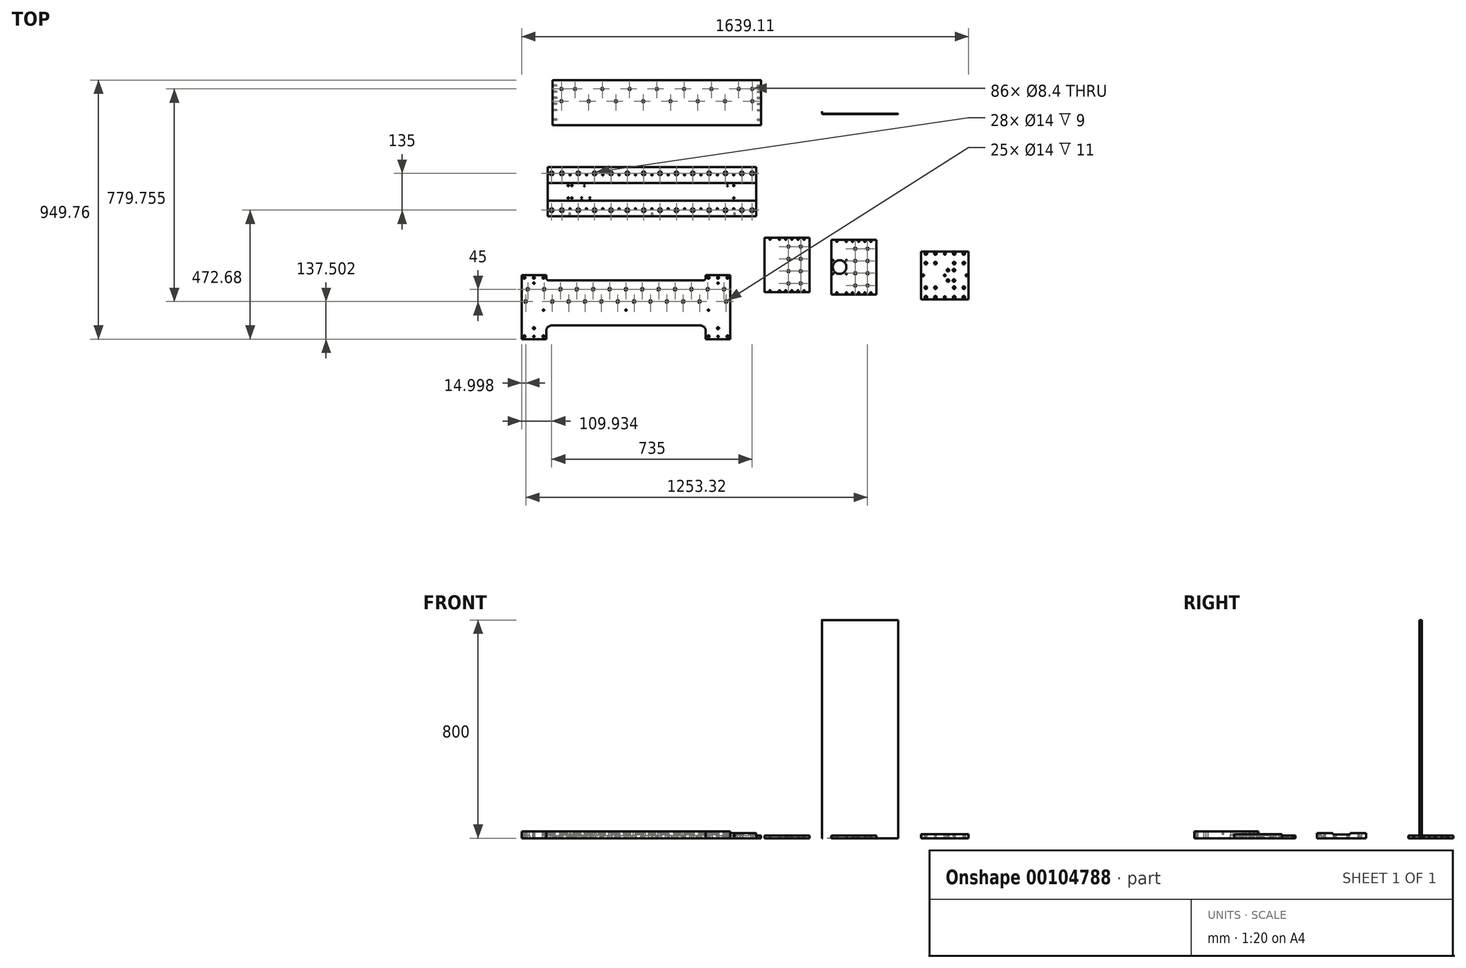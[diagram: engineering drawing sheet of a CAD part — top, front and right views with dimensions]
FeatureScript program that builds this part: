
annotation { "Feature Type Name" : "Feature", "Feature Type Description" : "" }
export const myFeature = defineFeature(function(context is Context, id is Id, definition is map)
    precondition{}
    {
        {
            var Q0;
            Q0=qCreatedBy(makeId("Top.planeOp"),FACE);
            var sketch = newSketch(context, id + "F0", { "sketchPlane" : qUnion([Q0])});
            skLineSegment(sketch, "E0.bottom", {"start": v(-320.38, 63) * mm, "end": v(444.62, 63) * mm});
            skLineSegment(sketch, "E0.top", {"start": v(-320.38, -117) * mm, "end": v(444.62, -117) * mm});
            skLineSegment(sketch, "E0.left", {"start": v(-320.38, 63) * mm, "end": v(-320.38, -117) * mm});
            skLineSegment(sketch, "E0.right", {"start": v(444.62, 63) * mm, "end": v(444.62, -117) * mm});
            skLineSegment(sketch, "E1.right", {"start": v(462.93, 382.58) * mm, "end": v(462.93, 217.58) * mm});
            skLineSegment(sketch, "E1.left", {"start": v(-302.07, 382.58) * mm, "end": v(-302.07, 217.58) * mm});
            skLineSegment(sketch, "E1.top", {"start": v(-302.07, 217.58) * mm, "end": v(462.93, 217.58) * mm});
            skLineSegment(sketch, "E1.bottom", {"start": v(-302.07, 382.58) * mm, "end": v(462.93, 382.58) * mm});
            skLineSegment(sketch, "E2.bottom", {"start": v(475.41, -195.5) * mm, "end": v(640.41, -195.5) * mm});
            skLineSegment(sketch, "E2.top", {"start": v(475.41, -395.5) * mm, "end": v(640.41, -395.5) * mm});
            skLineSegment(sketch, "E2.left", {"start": v(475.41, -195.5) * mm, "end": v(475.41, -395.5) * mm});
            skLineSegment(sketch, "E2.right", {"start": v(640.41, -195.5) * mm, "end": v(640.41, -395.5) * mm});
            skCircle(sketch, "E3", {"center": v(575.41, -200.5) * mm, "radius": 2.65 * mm});
            skCircle(sketch, "E4", {"center": v(620.41, -200.5) * mm, "radius": 2.65 * mm});
            skCircle(sketch, "E5", {"center": v(597.91, -200.5) * mm, "radius": 2.65 * mm});
            skCircle(sketch, "E6", {"center": v(552.91, -200.5) * mm, "radius": 2.65 * mm});
            skCircle(sketch, "E7", {"center": v(495.41, -200.5) * mm, "radius": 2.65 * mm});
            skCircle(sketch, "E8", {"center": v(530.41, -200.5) * mm, "radius": 2.65 * mm});
            skCircle(sketch, "E9", {"center": v(575.41, -390.5) * mm, "radius": 2.65 * mm});
            skCircle(sketch, "E10", {"center": v(552.91, -390.5) * mm, "radius": 2.65 * mm});
            skCircle(sketch, "E11", {"center": v(597.91, -390.5) * mm, "radius": 2.65 * mm});
            skCircle(sketch, "E12", {"center": v(620.41, -390.5) * mm, "radius": 2.65 * mm});
            skCircle(sketch, "E13", {"center": v(530.41, -390.5) * mm, "radius": 2.65 * mm});
            skCircle(sketch, "E14", {"center": v(495.41, -390.5) * mm, "radius": 2.65 * mm});
            skLineSegment(sketch, "E15.top", {"start": v(720.5, -403.15) * mm, "end": v(885.5, -403.15) * mm});
            skLineSegment(sketch, "E15.bottom", {"start": v(720.5, -203.15) * mm, "end": v(885.5, -203.15) * mm});
            skLineSegment(sketch, "E15.right", {"start": v(885.5, -203.15) * mm, "end": v(885.5, -403.15) * mm});
            skLineSegment(sketch, "E15.left", {"start": v(720.5, -203.15) * mm, "end": v(720.5, -403.15) * mm});
            skCircle(sketch, "E16", {"center": v(843, -208.15) * mm, "radius": 2.65 * mm});
            skCircle(sketch, "E17", {"center": v(798, -398.15) * mm, "radius": 2.65 * mm});
            skCircle(sketch, "E18", {"center": v(865.5, -208.15) * mm, "radius": 2.65 * mm});
            skCircle(sketch, "E19", {"center": v(843, -398.15) * mm, "radius": 2.65 * mm});
            skCircle(sketch, "E20", {"center": v(775.5, -208.15) * mm, "radius": 2.65 * mm});
            skCircle(sketch, "E21", {"center": v(865.5, -398.15) * mm, "radius": 2.65 * mm});
            skCircle(sketch, "E22", {"center": v(798, -208.15) * mm, "radius": 2.65 * mm});
            skCircle(sketch, "E23", {"center": v(775.5, -398.15) * mm, "radius": 2.65 * mm});
            skCircle(sketch, "E24", {"center": v(740.5, -398.15) * mm, "radius": 2.65 * mm});
            skCircle(sketch, "E25", {"center": v(740.5, -208.15) * mm, "radius": 2.65 * mm});
            skCircle(sketch, "E26", {"center": v(820.5, -398.15) * mm, "radius": 2.65 * mm});
            skCircle(sketch, "E27", {"center": v(820.5, -208.15) * mm, "radius": 2.65 * mm});
            skCircle(sketch, "E28", {"center": v(-237.88, -89.5) * mm, "radius": 2.5 * mm});
            skCircle(sketch, "E29", {"center": v(-177.88, -89.5) * mm, "radius": 2.5 * mm});
            skCircle(sketch, "E30", {"center": v(-117.88, -89.5) * mm, "radius": 2.5 * mm});
            skCircle(sketch, "E31", {"center": v(-57.88, -89.5) * mm, "radius": 2.5 * mm});
            skCircle(sketch, "E32", {"center": v(2.12, -89.5) * mm, "radius": 2.5 * mm});
            skCircle(sketch, "E33", {"center": v(62.12, -89.5) * mm, "radius": 2.5 * mm});
            skCircle(sketch, "E34", {"center": v(122.12, -89.5) * mm, "radius": 2.5 * mm});
            skCircle(sketch, "E35", {"center": v(182.12, -89.5) * mm, "radius": 2.5 * mm});
            skCircle(sketch, "E36", {"center": v(242.12, -89.5) * mm, "radius": 2.5 * mm});
            skCircle(sketch, "E37", {"center": v(302.12, -89.5) * mm, "radius": 2.5 * mm});
            skCircle(sketch, "E38", {"center": v(362.12, -89.5) * mm, "radius": 2.5 * mm});
            skCircle(sketch, "E39", {"center": v(-117.88, 35.5) * mm, "radius": 2.5 * mm});
            skCircle(sketch, "E40", {"center": v(-57.88, 35.5) * mm, "radius": 2.5 * mm});
            skCircle(sketch, "E41", {"center": v(182.12, 35.5) * mm, "radius": 2.5 * mm});
            skCircle(sketch, "E42", {"center": v(2.12, 35.5) * mm, "radius": 2.5 * mm});
            skCircle(sketch, "E43", {"center": v(62.12, 35.5) * mm, "radius": 2.5 * mm});
            skCircle(sketch, "E44", {"center": v(302.12, 35.5) * mm, "radius": 2.5 * mm});
            skCircle(sketch, "E45", {"center": v(-177.88, 35.5) * mm, "radius": 2.5 * mm});
            skCircle(sketch, "E46", {"center": v(362.12, 35.5) * mm, "radius": 2.5 * mm});
            skCircle(sketch, "E47", {"center": v(122.12, 35.5) * mm, "radius": 2.5 * mm});
            skCircle(sketch, "E48", {"center": v(242.12, 35.5) * mm, "radius": 2.5 * mm});
            skCircle(sketch, "E49", {"center": v(-237.88, 35.5) * mm, "radius": 2.5 * mm});
            skCircle(sketch, "E50", {"center": v(362.62, -4) * mm, "radius": 2.5 * mm});
            skCircle(sketch, "E51", {"center": v(362.62, -50) * mm, "radius": 2.5 * mm});
            skPoint(sketch, "E52", {"position": v(444.62, -27) * mm});
            skCircle(sketch, "E53", {"center": v(-244.38, -4) * mm, "radius": 2.5 * mm});
            skCircle(sketch, "E54", {"center": v(-244.38, -50) * mm, "radius": 2.5 * mm});
            skCircle(sketch, "E55", {"center": v(-231.38, -4) * mm, "radius": 2.5 * mm});
            skCircle(sketch, "E56", {"center": v(-231.38, -50) * mm, "radius": 2.5 * mm});
            skPoint(sketch, "E57", {"position": v(-320.38, -27) * mm});
            skLineSegment(sketch, "E58.bottom", {"start": v(1048.8, -246.02) * mm, "end": v(1223.8, -246.02) * mm});
            skLineSegment(sketch, "E58.top", {"start": v(1048.8, -421.02) * mm, "end": v(1223.8, -421.02) * mm});
            skLineSegment(sketch, "E58.left", {"start": v(1048.8, -246.02) * mm, "end": v(1048.8, -421.02) * mm});
            skLineSegment(sketch, "E58.right", {"start": v(1223.8, -246.02) * mm, "end": v(1223.8, -421.02) * mm});
            skCircle(sketch, "E59", {"center": v(1066.8, -253.52) * mm, "radius": 2.65 * mm});
            skCircle(sketch, "E60", {"center": v(1101.8, -253.52) * mm, "radius": 2.65 * mm});
            skCircle(sketch, "E61", {"center": v(1066.8, -288.52) * mm, "radius": 2.65 * mm});
            skCircle(sketch, "E62", {"center": v(1101.8, -288.52) * mm, "radius": 2.65 * mm});
            skCircle(sketch, "E63", {"center": v(1170.8, -253.52) * mm, "radius": 2.65 * mm});
            skCircle(sketch, "E64", {"center": v(1205.8, -288.52) * mm, "radius": 2.65 * mm});
            skCircle(sketch, "E65", {"center": v(1170.8, -288.52) * mm, "radius": 2.65 * mm});
            skCircle(sketch, "E66", {"center": v(1205.8, -253.52) * mm, "radius": 2.65 * mm});
            skCircle(sketch, "E67", {"center": v(1066.8, -378.52) * mm, "radius": 2.65 * mm});
            skCircle(sketch, "E68", {"center": v(1101.8, -413.52) * mm, "radius": 2.65 * mm});
            skCircle(sketch, "E69", {"center": v(1066.8, -413.52) * mm, "radius": 2.65 * mm});
            skCircle(sketch, "E70", {"center": v(1101.8, -378.52) * mm, "radius": 2.65 * mm});
            skCircle(sketch, "E71", {"center": v(1170.8, -378.52) * mm, "radius": 2.65 * mm});
            skCircle(sketch, "E72", {"center": v(1205.8, -413.52) * mm, "radius": 2.65 * mm});
            skCircle(sketch, "E73", {"center": v(1170.8, -413.52) * mm, "radius": 2.65 * mm});
            skCircle(sketch, "E74", {"center": v(1205.8, -378.52) * mm, "radius": 2.65 * mm});
            skPoint(sketch, "E75", {"position": v(1048.8, -333.52) * mm});
            skPoint(sketch, "E76", {"position": v(1136.3, -421.02) * mm});
            skCircle(sketch, "E77", {"center": v(1056.8, -333.52) * mm, "radius": 3.35 * mm});
            skCircle(sketch, "E78", {"center": v(1215.8, -333.52) * mm, "radius": 3.35 * mm});
            skCircle(sketch, "E79", {"center": v(1136.3, -413.02) * mm, "radius": 3.35 * mm});
            skCircle(sketch, "E80", {"center": v(1136.3, -254.02) * mm, "radius": 3.35 * mm});
            skCircle(sketch, "E81", {"center": v(1136.3, -333.52) * mm, "radius": 3 * mm});
            skCircle(sketch, "E82", {"center": v(1147.8, -314.52) * mm, "radius": 2.65 * mm});
            skCircle(sketch, "E83", {"center": v(1169.8, -314.52) * mm, "radius": 2.65 * mm});
            skCircle(sketch, "E84", {"center": v(1147.8, -352.52) * mm, "radius": 2.65 * mm});
            skCircle(sketch, "E85", {"center": v(1169.8, -352.52) * mm, "radius": 2.65 * mm});
            skCircle(sketch, "E86", {"center": v(1147.8, -314.52) * mm, "radius": 4.75 * mm});
            skCircle(sketch, "E87", {"center": v(1169.8, -314.52) * mm, "radius": 4.75 * mm});
            skCircle(sketch, "E88", {"center": v(1147.8, -352.52) * mm, "radius": 4.75 * mm});
            skCircle(sketch, "E89", {"center": v(1169.8, -352.52) * mm, "radius": 4.75 * mm});
            skCircle(sketch, "E90", {"center": v(1066.8, -253.52) * mm, "radius": 4.75 * mm});
            skCircle(sketch, "E91", {"center": v(1101.8, -253.52) * mm, "radius": 4.75 * mm});
            skCircle(sketch, "E92", {"center": v(1066.8, -288.52) * mm, "radius": 4.75 * mm});
            skCircle(sketch, "E93", {"center": v(1101.8, -288.52) * mm, "radius": 4.75 * mm});
            skCircle(sketch, "E94", {"center": v(1170.8, -253.52) * mm, "radius": 4.75 * mm});
            skCircle(sketch, "E95", {"center": v(1205.8, -253.52) * mm, "radius": 4.75 * mm});
            skCircle(sketch, "E96", {"center": v(1170.8, -288.52) * mm, "radius": 4.75 * mm});
            skCircle(sketch, "E97", {"center": v(1205.8, -288.52) * mm, "radius": 4.75 * mm});
            skCircle(sketch, "E98", {"center": v(1066.8, -378.52) * mm, "radius": 4.75 * mm});
            skCircle(sketch, "E99", {"center": v(1101.8, -378.52) * mm, "radius": 4.75 * mm});
            skCircle(sketch, "E100", {"center": v(1066.8, -413.52) * mm, "radius": 4.75 * mm});
            skCircle(sketch, "E101", {"center": v(1101.8, -413.52) * mm, "radius": 4.75 * mm});
            skCircle(sketch, "E102", {"center": v(1170.8, -413.52) * mm, "radius": 4.75 * mm});
            skCircle(sketch, "E103", {"center": v(1205.8, -413.52) * mm, "radius": 4.75 * mm});
            skCircle(sketch, "E104", {"center": v(1205.8, -378.52) * mm, "radius": 4.75 * mm});
            skCircle(sketch, "E105", {"center": v(1170.8, -378.52) * mm, "radius": 4.75 * mm});
            skLineSegment(sketch, "E106", {"start": v(-415.31, -332.18) * mm, "end": v(-415.31, -567.18) * mm});
            skLineSegment(sketch, "E107", {"start": v(-415.31, -567.18) * mm, "end": v(-325.31, -567.18) * mm});
            skLineSegment(sketch, "E108", {"start": v(-325.31, -567.18) * mm, "end": v(-325.31, -537.18) * mm});
            skLineSegment(sketch, "E109", {"start": v(-305.31, -517.18) * mm, "end": v(239.69, -517.18) * mm});
            skLineSegment(sketch, "E110", {"start": v(259.69, -537.18) * mm, "end": v(259.69, -567.18) * mm});
            skLineSegment(sketch, "E111", {"start": v(259.69, -567.18) * mm, "end": v(349.69, -567.18) * mm});
            skLineSegment(sketch, "E112", {"start": v(349.69, -567.18) * mm, "end": v(349.69, -332.18) * mm});
            skLineSegment(sketch, "E113", {"start": v(349.69, -332.18) * mm, "end": v(259.69, -332.18) * mm});
            skLineSegment(sketch, "E114", {"start": v(-325.31, -332.18) * mm, "end": v(-415.31, -332.18) * mm});
            skPoint(sketch, "E115.visualSharp", {"position": v(-325.31, -352.18) * mm});
            skPoint(sketch, "E116.visualSharp", {"position": v(259.69, -352.18) * mm});
            skPoint(sketch, "E117.visualSharp", {"position": v(259.69, -517.18) * mm});
            skArc(sketch, "E117.filletArc", {"start": v(259.69, -537.18) * mm, "mid": v(253.83, -523.04) * mm, "end": v(239.69, -517.18) * mm});
            skPoint(sketch, "E118.visualSharp", {"position": v(-325.31, -517.18) * mm});
            skArc(sketch, "E118.filletArc", {"start": v(-305.31, -517.18) * mm, "mid": v(-319.45, -523.04) * mm, "end": v(-325.31, -537.18) * mm});
            skLineSegment(sketch, "E119", {"start": v(685.49, 267.96) * mm, "end": v(685.49, 260.96) * mm});
            skLineSegment(sketch, "E120", {"start": v(688.49, 257.96) * mm, "end": v(965.49, 257.96) * mm});
            skLineSegment(sketch, "E121", {"start": v(965.49, 257.96) * mm, "end": v(965.49, 258.96) * mm});
            skLineSegment(sketch, "E122", {"start": v(965.49, 258.96) * mm, "end": v(689.49, 258.96) * mm});
            skLineSegment(sketch, "E123", {"start": v(686.49, 261.96) * mm, "end": v(686.49, 267.96) * mm});
            skLineSegment(sketch, "E124", {"start": v(686.49, 267.96) * mm, "end": v(685.49, 267.96) * mm});
            skPoint(sketch, "E125.visualSharp", {"position": v(686.49, 258.96) * mm});
            skArc(sketch, "E125.filletArc", {"start": v(686.49, 261.96) * mm, "mid": v(687.37, 259.84) * mm, "end": v(689.49, 258.96) * mm});
            skPoint(sketch, "E126.visualSharp", {"position": v(685.49, 257.96) * mm});
            skArc(sketch, "E126.filletArc", {"start": v(685.49, 260.96) * mm, "mid": v(686.37, 258.84) * mm, "end": v(688.49, 257.96) * mm});
            skPoint(sketch, "E127", {"position": v(750.5, -303.15) * mm});
            skArc(sketch, "E128", {"start": v(725.76, -327.9) * mm, "mid": v(754.77, -337.89) * mm, "end": v(780.5, -321.18) * mm});
            skPoint(sketch, "E129", {"position": v(725.76, -278.4) * mm});
            skPoint(sketch, "E130", {"position": v(725.76, -327.9) * mm});
            skPoint(sketch, "E131", {"position": v(775.26, -278.4) * mm});
            skPoint(sketch, "E132", {"position": v(775.26, -327.9) * mm});
            skArc(sketch, "E133.trimOffspring", {"start": v(780.4, -284.95) * mm, "mid": v(754.67, -268.4) * mm, "end": v(725.76, -278.4) * mm});
            skLineSegment(sketch, "E134", {"start": v(750.5, -303.15) * mm, "end": v(720.5, -303.15) * mm});
            skPoint(sketch, "E135", {"position": v(808, -235.65) * mm});
            skPoint(sketch, "E136", {"position": v(853, -235.65) * mm});
            skPoint(sketch, "E137", {"position": v(808, -280.65) * mm});
            skPoint(sketch, "E138", {"position": v(853, -280.65) * mm});
            skPoint(sketch, "E139", {"position": v(853, -325.65) * mm});
            skPoint(sketch, "E140", {"position": v(808, -325.65) * mm});
            skPoint(sketch, "E141", {"position": v(808, -370.65) * mm});
            skPoint(sketch, "E142", {"position": v(853, -370.65) * mm});
            skLineSegment(sketch, "E143", {"start": v(725.76, -327.9) * mm, "end": v(750.5, -303.15) * mm});
            skPoint(sketch, "E144", {"position": v(562.91, -228) * mm});
            skPoint(sketch, "E145", {"position": v(562.91, -273) * mm});
            skPoint(sketch, "E146", {"position": v(562.91, -318) * mm});
            skPoint(sketch, "E147", {"position": v(562.91, -363) * mm});
            skPoint(sketch, "E148", {"position": v(607.91, -363) * mm});
            skPoint(sketch, "E149", {"position": v(607.91, -318) * mm});
            skPoint(sketch, "E150", {"position": v(607.91, -273) * mm});
            skPoint(sketch, "E151", {"position": v(607.91, -228) * mm});
            skLineSegment(sketch, "E152", {"start": v(-325.31, -332.18) * mm, "end": v(-325.31, -342.18) * mm});
            skLineSegment(sketch, "E153", {"start": v(-315.31, -352.18) * mm, "end": v(249.69, -352.18) * mm});
            skLineSegment(sketch, "E154", {"start": v(259.69, -332.18) * mm, "end": v(259.69, -342.18) * mm});
            skPoint(sketch, "E155", {"position": v(-32.81, -352.18) * mm});
            skPoint(sketch, "E156", {"position": v(-32.81, -517.18) * mm});
            skArc(sketch, "E157.filletArc", {"start": v(-325.31, -342.18) * mm, "mid": v(-322.38, -349.25) * mm, "end": v(-315.31, -352.18) * mm});
            skArc(sketch, "E158.filletArc", {"start": v(249.69, -352.18) * mm, "mid": v(256.76, -349.25) * mm, "end": v(259.69, -342.18) * mm});
            skSolve(sketch);
        }
        {
            var Q0;
            Q0=makeQuery(id+"F0.imprint","IMPRINT",FACE,{"disambiguationData":[TD([[makeQuery(id+"F0.imprint","IMPRINT",EDGE,{"derivedFrom":sQuery(id+"F0.wireOp",EDGE,"E0.bottom")}),-1.0]])]});
            var Q1;
            Q1=makeQuery(id+"F0.imprint","IMPRINT",FACE,{"disambiguationData":[TD([[makeQuery(id+"F0.imprint","IMPRINT",EDGE,{"derivedFrom":sQuery(id+"F0.wireOp",EDGE,"E50")}),-1.0]])]});
            extrude(context, id + "F1", {"entities" : qUnion([Q0, Q1]), "depth" : 18 * mm});
        }
        {
            var Q0;
            Q0=makeQuery(id+"F0.imprint","IMPRINT",FACE,{"disambiguationData":[TD([[makeQuery(id+"F0.imprint","IMPRINT",EDGE,{"derivedFrom":sQuery(id+"F0.wireOp",EDGE,"E1.right")}),-1.0]])]});
            extrude(context, id + "F2", {"entities" : qUnion([Q0]), "depth" : 10 * mm});
        }
        {
            var Q0;
            Q0=makeQuery(id+"F2.opExtrude","CAP_FACE",FACE,{"disambiguationData":[OSD([sQuery(id+"F0.wireOp",EDGE,"E1.right"),sQuery(id+"F0.wireOp",EDGE,"E1.left"),sQuery(id+"F0.wireOp",EDGE,"E1.top"),sQuery(id+"F0.wireOp",EDGE,"E1.bottom")])],"isStart":false});
            var sketch = newSketch(context, id + "F3", { "sketchPlane" : qUnion([Q0])});
            skLineSegment(sketch, "E159", {"start": v(-296.1, 350.08) * mm, "end": v(454.82, 350.08) * mm});
            skPoint(sketch, "E160", {"position": v(80.43, 350.08) * mm});
            skPoint(sketch, "E161", {"position": v(-19.57, 350.08) * mm});
            skPoint(sketch, "E162", {"position": v(-119.57, 350.08) * mm});
            skPoint(sketch, "E163", {"position": v(-219.57, 350.08) * mm});
            skPoint(sketch, "E164", {"position": v(-269.57, 350.08) * mm});
            skPoint(sketch, "E165", {"position": v(180.43, 350.08) * mm});
            skPoint(sketch, "E166", {"position": v(280.43, 350.08) * mm});
            skPoint(sketch, "E167", {"position": v(380.43, 350.08) * mm});
            skPoint(sketch, "E168", {"position": v(430.43, 350.08) * mm});
            skLineSegment(sketch, "E169", {"start": v(-295.03, 305.08) * mm, "end": v(456.43, 305.08) * mm});
            skPoint(sketch, "E170", {"position": v(130.43, 305.08) * mm});
            skPoint(sketch, "E171", {"position": v(30.43, 305.08) * mm});
            skPoint(sketch, "E172", {"position": v(-69.57, 305.08) * mm});
            skPoint(sketch, "E173", {"position": v(-169.57, 305.08) * mm});
            skPoint(sketch, "E174", {"position": v(-269.57, 305.08) * mm});
            skPoint(sketch, "E175", {"position": v(230.43, 305.08) * mm});
            skPoint(sketch, "E176", {"position": v(330.43, 305.08) * mm});
            skPoint(sketch, "E177", {"position": v(430.43, 305.08) * mm});
            skSolve(sketch);
        }
        {
            var Q0;
            Q0=makeQuery(id+"F2.opExtrude","SWEPT_FACE",FACE,{"disambiguationData":[OSD([sQuery(id+"F0.wireOp",EDGE,"E1.right")])]});
            var sketch = newSketch(context, id + "F4", { "sketchPlane" : qUnion([Q0])});
            skCircle(sketch, "E178", {"center": v(272.58, 5) * mm, "radius": 2.1 * mm});
            skCircle(sketch, "E179", {"center": v(237.58, 5) * mm, "radius": 2.1 * mm});
            skCircle(sketch, "E180", {"center": v(295.08, 5) * mm, "radius": 2.1 * mm});
            skCircle(sketch, "E181", {"center": v(317.58, 5) * mm, "radius": 2.1 * mm});
            skCircle(sketch, "E182", {"center": v(340.08, 5) * mm, "radius": 2.1 * mm});
            skCircle(sketch, "E183", {"center": v(362.58, 5) * mm, "radius": 2.1 * mm});
            skSolve(sketch);
        }
        {
            var Q0;
            Q0=makeQuery(id+"F4.imprint","IMPRINT",FACE,{"disambiguationData":[TD([[makeQuery(id+"F4.imprint","IMPRINT",EDGE,{"derivedFrom":sQuery(id+"F4.wireOp",EDGE,"E179")}),1.0]])]});
            var Q1;
            Q1=makeQuery(id+"F4.imprint","IMPRINT",FACE,{"disambiguationData":[TD([[makeQuery(id+"F4.imprint","IMPRINT",EDGE,{"derivedFrom":sQuery(id+"F4.wireOp",EDGE,"E178")}),1.0]])]});
            var Q2;
            Q2=makeQuery(id+"F4.imprint","IMPRINT",FACE,{"disambiguationData":[TD([[makeQuery(id+"F4.imprint","IMPRINT",EDGE,{"derivedFrom":sQuery(id+"F4.wireOp",EDGE,"E180")}),1.0]])]});
            var Q3;
            Q3=makeQuery(id+"F4.imprint","IMPRINT",FACE,{"disambiguationData":[TD([[makeQuery(id+"F4.imprint","IMPRINT",EDGE,{"derivedFrom":sQuery(id+"F4.wireOp",EDGE,"E181")}),1.0]])]});
            var Q4;
            Q4=makeQuery(id+"F4.imprint","IMPRINT",FACE,{"disambiguationData":[TD([[makeQuery(id+"F4.imprint","IMPRINT",EDGE,{"derivedFrom":sQuery(id+"F4.wireOp",EDGE,"E182")}),1.0]])]});
            var Q5;
            Q5=makeQuery(id+"F4.imprint","IMPRINT",FACE,{"disambiguationData":[TD([[makeQuery(id+"F4.imprint","IMPRINT",EDGE,{"derivedFrom":sQuery(id+"F4.wireOp",EDGE,"E183")}),1.0]])]});
            extrude(context, id + "F5", {"entities" : qUnion([Q0, Q1, Q2, Q3, Q4, Q5]), "operationType" : NewBodyOperationType.REMOVE, "oppositeDirection" : true, "depth" : 15 * mm});
        }
        {
            var Q0;
            Q0=makeQuery(id+"F2.opExtrude","SWEPT_FACE",FACE,{"disambiguationData":[OSD([sQuery(id+"F0.wireOp",EDGE,"E1.left")])]});
            var sketch = newSketch(context, id + "F6", { "sketchPlane" : qUnion([Q0])});
            skCircle(sketch, "E184", {"center": v(-295.08, 5) * mm, "radius": 2.1 * mm});
            skCircle(sketch, "E185", {"center": v(-272.58, 5) * mm, "radius": 2.1 * mm});
            skCircle(sketch, "E186", {"center": v(-237.58, 5) * mm, "radius": 2.1 * mm});
            skCircle(sketch, "E187", {"center": v(-340.08, 5) * mm, "radius": 2.1 * mm});
            skCircle(sketch, "E188", {"center": v(-362.58, 5) * mm, "radius": 2.1 * mm});
            skCircle(sketch, "E189", {"center": v(-317.58, 5) * mm, "radius": 2.1 * mm});
            skSolve(sketch);
        }
        {
            var Q0;
            Q0=makeQuery(id+"F6.imprint","IMPRINT",FACE,{"disambiguationData":[TD([[makeQuery(id+"F6.imprint","IMPRINT",EDGE,{"derivedFrom":sQuery(id+"F6.wireOp",EDGE,"E186")}),1.0]])]});
            var Q1;
            Q1=makeQuery(id+"F6.imprint","IMPRINT",FACE,{"disambiguationData":[TD([[makeQuery(id+"F6.imprint","IMPRINT",EDGE,{"derivedFrom":sQuery(id+"F6.wireOp",EDGE,"E185")}),1.0]])]});
            var Q2;
            Q2=makeQuery(id+"F6.imprint","IMPRINT",FACE,{"disambiguationData":[TD([[makeQuery(id+"F6.imprint","IMPRINT",EDGE,{"derivedFrom":sQuery(id+"F6.wireOp",EDGE,"E184")}),1.0]])]});
            var Q3;
            Q3=makeQuery(id+"F6.imprint","IMPRINT",FACE,{"disambiguationData":[TD([[makeQuery(id+"F6.imprint","IMPRINT",EDGE,{"derivedFrom":sQuery(id+"F6.wireOp",EDGE,"E189")}),1.0]])]});
            var Q4;
            Q4=makeQuery(id+"F6.imprint","IMPRINT",FACE,{"disambiguationData":[TD([[makeQuery(id+"F6.imprint","IMPRINT",EDGE,{"derivedFrom":sQuery(id+"F6.wireOp",EDGE,"E187")}),1.0]])]});
            var Q5;
            Q5=makeQuery(id+"F6.imprint","IMPRINT",FACE,{"disambiguationData":[TD([[makeQuery(id+"F6.imprint","IMPRINT",EDGE,{"derivedFrom":sQuery(id+"F6.wireOp",EDGE,"E188")}),1.0]])]});
            extrude(context, id + "F7", {"entities" : qUnion([Q0, Q1, Q2, Q3, Q4, Q5]), "operationType" : NewBodyOperationType.REMOVE, "oppositeDirection" : true, "depth" : 15 * mm});
        }
        {
            var Q0;
            Q0=makeQuery(id+"F0.imprint","IMPRINT",FACE,{"disambiguationData":[TD([[makeQuery(id+"F0.imprint","IMPRINT",EDGE,{"derivedFrom":sQuery(id+"F0.wireOp",EDGE,"E2.bottom")}),-1.0]])]});
            extrude(context, id + "F8", {"entities" : qUnion([Q0]), "depth" : 10 * mm});
        }
        {
            var Q0;
            Q0=makeQuery(id+"F0.imprint","IMPRINT",FACE,{"disambiguationData":[TD([[makeQuery(id+"F0.imprint","IMPRINT",EDGE,{"derivedFrom":sQuery(id+"F0.wireOp",EDGE,"E15.top")}),1.0]])]});
            extrude(context, id + "F9", {"entities" : qUnion([Q0]), "depth" : 10 * mm});
        }
        {
            var Q0;
            Q0=makeQuery(id+"F0.imprint","IMPRINT",FACE,{"disambiguationData":[TD([[makeQuery(id+"F0.imprint","IMPRINT",EDGE,{"derivedFrom":sQuery(id+"F0.wireOp",EDGE,"E58.bottom")}),-1.0]])]});
            extrude(context, id + "F10", {"entities" : qUnion([Q0]), "depth" : 15 * mm});
        }
        {
            var Q0;
            Q0=makeQuery(id+"F0.imprint","IMPRINT",FACE,{"disambiguationData":[TD([[makeQuery(id+"F0.imprint","IMPRINT",EDGE,{"derivedFrom":sQuery(id+"F0.wireOp",EDGE,"E82")}),-1.0]])]});
            var Q1;
            Q1=makeQuery(id+"F0.imprint","IMPRINT",FACE,{"disambiguationData":[TD([[makeQuery(id+"F0.imprint","IMPRINT",EDGE,{"derivedFrom":sQuery(id+"F0.wireOp",EDGE,"E83")}),-1.0]])]});
            var Q2;
            Q2=makeQuery(id+"F0.imprint","IMPRINT",FACE,{"disambiguationData":[TD([[makeQuery(id+"F0.imprint","IMPRINT",EDGE,{"derivedFrom":sQuery(id+"F0.wireOp",EDGE,"E84")}),-1.0]])]});
            var Q3;
            Q3=makeQuery(id+"F0.imprint","IMPRINT",FACE,{"disambiguationData":[TD([[makeQuery(id+"F0.imprint","IMPRINT",EDGE,{"derivedFrom":sQuery(id+"F0.wireOp",EDGE,"E85")}),-1.0]])]});
            extrude(context, id + "F11", {"entities" : qUnion([Q0, Q1, Q2, Q3]), "operationType" : NewBodyOperationType.ADD, "depth" : 9 * mm});
        }
        {
            var Q0;
            Q0=makeQuery(id+"F1.opExtrude","CAP_FACE",FACE,{"disambiguationData":[OSD([sQuery(id+"F0.wireOp",EDGE,"E0.bottom"),sQuery(id+"F0.wireOp",EDGE,"E0.top"),sQuery(id+"F0.wireOp",EDGE,"E0.left"),sQuery(id+"F0.wireOp",EDGE,"E0.right"),sQuery(id+"F0.wireOp",EDGE,"E28"),sQuery(id+"F0.wireOp",EDGE,"E29"),sQuery(id+"F0.wireOp",EDGE,"E30"),sQuery(id+"F0.wireOp",EDGE,"E31"),sQuery(id+"F0.wireOp",EDGE,"E32"),sQuery(id+"F0.wireOp",EDGE,"E33"),sQuery(id+"F0.wireOp",EDGE,"E34"),sQuery(id+"F0.wireOp",EDGE,"E35"),sQuery(id+"F0.wireOp",EDGE,"E36"),sQuery(id+"F0.wireOp",EDGE,"E37"),sQuery(id+"F0.wireOp",EDGE,"E38"),sQuery(id+"F0.wireOp",EDGE,"E39"),sQuery(id+"F0.wireOp",EDGE,"E40"),sQuery(id+"F0.wireOp",EDGE,"E41"),sQuery(id+"F0.wireOp",EDGE,"E42"),sQuery(id+"F0.wireOp",EDGE,"E43"),sQuery(id+"F0.wireOp",EDGE,"E44"),sQuery(id+"F0.wireOp",EDGE,"E45"),sQuery(id+"F0.wireOp",EDGE,"E46"),sQuery(id+"F0.wireOp",EDGE,"E47"),sQuery(id+"F0.wireOp",EDGE,"E48"),sQuery(id+"F0.wireOp",EDGE,"E49"),sQuery(id+"F0.wireOp",EDGE,"E50"),sQuery(id+"F0.wireOp",EDGE,"E51"),sQuery(id+"F0.wireOp",EDGE,"E53"),sQuery(id+"F0.wireOp",EDGE,"E54"),sQuery(id+"F0.wireOp",EDGE,"E55"),sQuery(id+"F0.wireOp",EDGE,"E56")])],"isStart":false});
            var sketch = newSketch(context, id + "F12", { "sketchPlane" : qUnion([Q0])});
            skLineSegment(sketch, "E190.bottom", {"start": v(-320.38, 5) * mm, "end": v(444.62, 5) * mm});
            skLineSegment(sketch, "E190.top", {"start": v(-320.38, -59) * mm, "end": v(444.62, -59) * mm});
            skLineSegment(sketch, "E190.right", {"start": v(444.62, 5) * mm, "end": v(444.62, -59) * mm});
            skLineSegment(sketch, "E190.left", {"start": v(-320.38, 5) * mm, "end": v(-320.38, -59) * mm});
            skSolve(sketch);
        }
        {
            var Q0;
            Q0=makeQuery(id+"F12.imprint","IMPRINT",FACE,{"disambiguationData":[TD([[makeQuery(id+"F12.imprint","IMPRINT",EDGE,{"derivedFrom":sQuery(id+"F12.wireOp",EDGE,"E190.bottom")}),-1.0]])]});
            extrude(context, id + "F13", {"entities" : qUnion([Q0]), "operationType" : NewBodyOperationType.REMOVE, "oppositeDirection" : true, "depth" : 5 * mm});
        }
        {
            var Q0;
            Q0=makeQuery(id+"F0.imprint","IMPRINT",FACE,{"disambiguationData":[TD([[makeQuery(id+"F0.imprint","IMPRINT",EDGE,{"derivedFrom":sQuery(id+"F0.wireOp",EDGE,"E59")}),-1.0]])]});
            var Q1;
            Q1=makeQuery(id+"F0.imprint","IMPRINT",FACE,{"disambiguationData":[TD([[makeQuery(id+"F0.imprint","IMPRINT",EDGE,{"derivedFrom":sQuery(id+"F0.wireOp",EDGE,"E60")}),-1.0]])]});
            var Q2;
            Q2=makeQuery(id+"F0.imprint","IMPRINT",FACE,{"disambiguationData":[TD([[makeQuery(id+"F0.imprint","IMPRINT",EDGE,{"derivedFrom":sQuery(id+"F0.wireOp",EDGE,"E61")}),-1.0]])]});
            var Q3;
            Q3=makeQuery(id+"F0.imprint","IMPRINT",FACE,{"disambiguationData":[TD([[makeQuery(id+"F0.imprint","IMPRINT",EDGE,{"derivedFrom":sQuery(id+"F0.wireOp",EDGE,"E62")}),-1.0]])]});
            var Q4;
            Q4=makeQuery(id+"F0.imprint","IMPRINT",FACE,{"disambiguationData":[TD([[makeQuery(id+"F0.imprint","IMPRINT",EDGE,{"derivedFrom":sQuery(id+"F0.wireOp",EDGE,"E63")}),-1.0]])]});
            var Q5;
            Q5=makeQuery(id+"F0.imprint","IMPRINT",FACE,{"disambiguationData":[TD([[makeQuery(id+"F0.imprint","IMPRINT",EDGE,{"derivedFrom":sQuery(id+"F0.wireOp",EDGE,"E66")}),-1.0]])]});
            var Q6;
            Q6=makeQuery(id+"F0.imprint","IMPRINT",FACE,{"disambiguationData":[TD([[makeQuery(id+"F0.imprint","IMPRINT",EDGE,{"derivedFrom":sQuery(id+"F0.wireOp",EDGE,"E64")}),-1.0]])]});
            var Q7;
            Q7=makeQuery(id+"F0.imprint","IMPRINT",FACE,{"disambiguationData":[TD([[makeQuery(id+"F0.imprint","IMPRINT",EDGE,{"derivedFrom":sQuery(id+"F0.wireOp",EDGE,"E65")}),-1.0]])]});
            var Q8;
            Q8=makeQuery(id+"F0.imprint","IMPRINT",FACE,{"disambiguationData":[TD([[makeQuery(id+"F0.imprint","IMPRINT",EDGE,{"derivedFrom":sQuery(id+"F0.wireOp",EDGE,"E74")}),-1.0]])]});
            var Q9;
            Q9=makeQuery(id+"F0.imprint","IMPRINT",FACE,{"disambiguationData":[TD([[makeQuery(id+"F0.imprint","IMPRINT",EDGE,{"derivedFrom":sQuery(id+"F0.wireOp",EDGE,"E71")}),-1.0]])]});
            var Q10;
            Q10=makeQuery(id+"F0.imprint","IMPRINT",FACE,{"disambiguationData":[TD([[makeQuery(id+"F0.imprint","IMPRINT",EDGE,{"derivedFrom":sQuery(id+"F0.wireOp",EDGE,"E73")}),-1.0]])]});
            var Q11;
            Q11=makeQuery(id+"F0.imprint","IMPRINT",FACE,{"disambiguationData":[TD([[makeQuery(id+"F0.imprint","IMPRINT",EDGE,{"derivedFrom":sQuery(id+"F0.wireOp",EDGE,"E72")}),-1.0]])]});
            var Q12;
            Q12=makeQuery(id+"F0.imprint","IMPRINT",FACE,{"disambiguationData":[TD([[makeQuery(id+"F0.imprint","IMPRINT",EDGE,{"derivedFrom":sQuery(id+"F0.wireOp",EDGE,"E67")}),-1.0]])]});
            var Q13;
            Q13=makeQuery(id+"F0.imprint","IMPRINT",FACE,{"disambiguationData":[TD([[makeQuery(id+"F0.imprint","IMPRINT",EDGE,{"derivedFrom":sQuery(id+"F0.wireOp",EDGE,"E70")}),-1.0]])]});
            var Q14;
            Q14=makeQuery(id+"F0.imprint","IMPRINT",FACE,{"disambiguationData":[TD([[makeQuery(id+"F0.imprint","IMPRINT",EDGE,{"derivedFrom":sQuery(id+"F0.wireOp",EDGE,"E68")}),-1.0]])]});
            var Q15;
            Q15=makeQuery(id+"F0.imprint","IMPRINT",FACE,{"disambiguationData":[TD([[makeQuery(id+"F0.imprint","IMPRINT",EDGE,{"derivedFrom":sQuery(id+"F0.wireOp",EDGE,"E69")}),-1.0]])]});
            extrude(context, id + "F14", {"entities" : qUnion([Q0, Q1, Q2, Q3, Q4, Q5, Q6, Q7, Q8, Q9, Q10, Q11, Q12, Q13, Q14, Q15]), "operationType" : NewBodyOperationType.ADD, "depth" : 9.3 * mm});
        }
        {
            var Q0;
            Q0=makeQuery(id+"F0.imprint","IMPRINT",FACE,{"disambiguationData":[TD([[makeQuery(id+"F0.imprint","IMPRINT",EDGE,{"derivedFrom":sQuery(id+"F0.wireOp",EDGE,"E106")}),1.0]])]});
            extrude(context, id + "F15", {"entities" : qUnion([Q0]), "depth" : 25 * mm});
        }
        {
            var Q0;
            Q0=makeQuery(id+"F15.opExtrude","CAP_FACE",FACE,{"disambiguationData":[OSD([sQuery(id+"F0.wireOp",EDGE,"E106"),sQuery(id+"F0.wireOp",EDGE,"E107"),sQuery(id+"F0.wireOp",EDGE,"E108"),sQuery(id+"F0.wireOp",EDGE,"E109"),sQuery(id+"F0.wireOp",EDGE,"E110"),sQuery(id+"F0.wireOp",EDGE,"E111"),sQuery(id+"F0.wireOp",EDGE,"E112"),sQuery(id+"F0.wireOp",EDGE,"E113"),sQuery(id+"F0.wireOp",EDGE,"0buerCJm-Lt2G-jJo9-9LwQ-wygei9gSLH8x"),sQuery(id+"F0.wireOp",EDGE,"Cyo2l2n8-YYKy-Kl9p-W61Z-JTT53oPBxWLL"),sQuery(id+"F0.wireOp",EDGE,"L2AfWR9S-dHOE-b34O-2OkN-z4aWcMazjyWb"),sQuery(id+"F0.wireOp",EDGE,"E114"),sQuery(id+"F0.wireOp",EDGE,"E115.filletArc"),sQuery(id+"F0.wireOp",EDGE,"E116.filletArc"),sQuery(id+"F0.wireOp",EDGE,"E117.filletArc"),sQuery(id+"F0.wireOp",EDGE,"E118.filletArc")])],"isStart":false});
            var sketch = newSketch(context, id + "F16", { "sketchPlane" : qUnion([Q0])});
            skLineSegment(sketch, "E191", {"start": v(-410.42, -342.18) * mm, "end": v(-329.14, -342.18) * mm});
            skPoint(sketch, "E192", {"position": v(-370.31, -342.18) * mm});
            skPoint(sketch, "E192.positionSnap0", {"position": v(-370.31, -332.18) * mm});
            skPoint(sketch, "E193", {"position": v(-405.31, -342.18) * mm});
            skLineSegment(sketch, "E194", {"start": v(-407.79, -557.18) * mm, "end": v(-332.61, -557.18) * mm});
            skLineSegment(sketch, "E195", {"start": v(-405.31, -550.84) * mm, "end": v(-405.31, -571.5) * mm});
            skLineSegment(sketch, "E196", {"start": v(-335.31, -552.57) * mm, "end": v(-335.31, -571.67) * mm});
            skPoint(sketch, "E197", {"position": v(-370.31, -527.18) * mm});
            skPoint(sketch, "E197.positionSnap0", {"position": v(-370.31, -567.18) * mm});
            skPoint(sketch, "E198", {"position": v(-405.31, -557.18) * mm});
            skPoint(sketch, "E199", {"position": v(-335.31, -557.18) * mm});
            skLineSegment(sketch, "E200", {"start": v(263.02, -557.18) * mm, "end": v(345.47, -557.18) * mm});
            skLineSegment(sketch, "E201", {"start": v(269.69, -552.58) * mm, "end": v(269.69, -571.37) * mm});
            skLineSegment(sketch, "E202", {"start": v(339.69, -552.13) * mm, "end": v(339.69, -570.57) * mm});
            skPoint(sketch, "E203", {"position": v(304.69, -527.18) * mm});
            skPoint(sketch, "E203.positionSnap0", {"position": v(304.69, -567.18) * mm});
            skPoint(sketch, "E204", {"position": v(269.69, -557.18) * mm});
            skPoint(sketch, "E205", {"position": v(339.69, -557.18) * mm});
            skLineSegment(sketch, "E206", {"start": v(263.39, -342.18) * mm, "end": v(346.84, -342.18) * mm});
            skPoint(sketch, "E207", {"position": v(304.69, -342.18) * mm});
            skPoint(sketch, "E207.positionSnap0", {"position": v(304.69, -332.18) * mm});
            skPoint(sketch, "E208", {"position": v(339.69, -342.18) * mm});
            skPoint(sketch, "E209", {"position": v(-370.31, -362.18) * mm});
            skPoint(sketch, "E210", {"position": v(304.69, -362.18) * mm});
            skPoint(sketch, "E211", {"position": v(-335.31, -342.18) * mm});
            skPoint(sketch, "E212", {"position": v(269.69, -342.18) * mm});
            skPoint(sketch, "E213", {"position": v(-32.81, -461.18) * mm});
            skPoint(sketch, "E214", {"position": v(269.69, -461.18) * mm});
            skPoint(sketch, "E215", {"position": v(-335.31, -461.18) * mm});
            skPoint(sketch, "E216", {"position": v(-370.31, -557.18) * mm});
            skPoint(sketch, "E217", {"position": v(304.69, -557.18) * mm});
            skSolve(sketch);
        }
        {
            var Q0;
            Q0=sQuery(id+"F16.wireOp",VERTEX,"E193");
            var Q1;
            Q1=sQuery(id+"F16.wireOp",VERTEX,"E192");
            var Q2;
            Q2=sQuery(id+"F16.wireOp",VERTEX,"4b770387-a9b1-489f-a8f6-3e866c467a90");
            var Q3;
            Q3=sQuery(id+"F16.wireOp",VERTEX,"E198");
            var Q4;
            Q4=sQuery(id+"F16.wireOp",VERTEX,"E197");
            var Q5;
            Q5=sQuery(id+"F16.wireOp",VERTEX,"E199");
            var Q6;
            Q6=sQuery(id+"F16.wireOp",VERTEX,"E204");
            var Q7;
            Q7=sQuery(id+"F16.wireOp",VERTEX,"E203");
            var Q8;
            Q8=sQuery(id+"F16.wireOp",VERTEX,"E205");
            var Q9;
            Q9=sQuery(id+"F16.wireOp",VERTEX,"125a19e2-877c-440c-9ff0-02cc8aefc776");
            var Q10;
            Q10=sQuery(id+"F16.wireOp",VERTEX,"E207");
            var Q11;
            Q11=sQuery(id+"F16.wireOp",VERTEX,"E208");
            var Q12;
            Q12=sQuery(id+"F16.wireOp",VERTEX,"E211");
            var Q13;
            Q13=sQuery(id+"F16.wireOp",VERTEX,"E212");
            var Q14;
            Q14=makeQuery(id+"F15.opExtrude","SWEPT_BODY",BODY,{"disambiguationData":[OSD([sQuery(id+"F0.wireOp",EDGE,"E106"),sQuery(id+"F0.wireOp",EDGE,"E107"),sQuery(id+"F0.wireOp",EDGE,"E108"),sQuery(id+"F0.wireOp",EDGE,"E109"),sQuery(id+"F0.wireOp",EDGE,"E110"),sQuery(id+"F0.wireOp",EDGE,"E111"),sQuery(id+"F0.wireOp",EDGE,"E112"),sQuery(id+"F0.wireOp",EDGE,"E113"),sQuery(id+"F0.wireOp",EDGE,"0buerCJm-Lt2G-jJo9-9LwQ-wygei9gSLH8x"),sQuery(id+"F0.wireOp",EDGE,"Cyo2l2n8-YYKy-Kl9p-W61Z-JTT53oPBxWLL"),sQuery(id+"F0.wireOp",EDGE,"L2AfWR9S-dHOE-b34O-2OkN-z4aWcMazjyWb"),sQuery(id+"F0.wireOp",EDGE,"E114"),sQuery(id+"F0.wireOp",EDGE,"E115.filletArc"),sQuery(id+"F0.wireOp",EDGE,"E116.filletArc"),sQuery(id+"F0.wireOp",EDGE,"E117.filletArc"),sQuery(id+"F0.wireOp",EDGE,"E118.filletArc")])]});
            hole(context, id + "F17", {"style" : HoleStyle.SIMPLE, "endStyle" : HoleEndStyle.THROUGH, "holeDiameter" : 7.5 * mm, "locations" : qUnion([Q0, Q1, Q2, Q3, Q4, Q5, Q6, Q7, Q8, Q9, Q10, Q11, Q12, Q13]), "scope" : qUnion([Q14]), "tappedDepth" : 12 * mm, "tapClearance" : 3});
        }
        {
            var Q0;
            Q0=sQuery(id+"F16.wireOp",VERTEX,"E209");
            var Q1;
            Q1=sQuery(id+"F16.wireOp",VERTEX,"E210");
            var Q2;
            Q2=sQuery(id+"F16.wireOp",VERTEX,"E216");
            var Q3;
            Q3=sQuery(id+"F16.wireOp",VERTEX,"E217");
            var Q4;
            Q4=makeQuery(id+"F15.opExtrude","SWEPT_BODY",BODY,{"disambiguationData":[OSD([sQuery(id+"F0.wireOp",EDGE,"E106"),sQuery(id+"F0.wireOp",EDGE,"E107"),sQuery(id+"F0.wireOp",EDGE,"E108"),sQuery(id+"F0.wireOp",EDGE,"E109"),sQuery(id+"F0.wireOp",EDGE,"E110"),sQuery(id+"F0.wireOp",EDGE,"E111"),sQuery(id+"F0.wireOp",EDGE,"E112"),sQuery(id+"F0.wireOp",EDGE,"E113"),sQuery(id+"F0.wireOp",EDGE,"0buerCJm-Lt2G-jJo9-9LwQ-wygei9gSLH8x"),sQuery(id+"F0.wireOp",EDGE,"Cyo2l2n8-YYKy-Kl9p-W61Z-JTT53oPBxWLL"),sQuery(id+"F0.wireOp",EDGE,"L2AfWR9S-dHOE-b34O-2OkN-z4aWcMazjyWb"),sQuery(id+"F0.wireOp",EDGE,"E114"),sQuery(id+"F0.wireOp",EDGE,"E115.filletArc"),sQuery(id+"F0.wireOp",EDGE,"E116.filletArc"),sQuery(id+"F0.wireOp",EDGE,"E117.filletArc"),sQuery(id+"F0.wireOp",EDGE,"E118.filletArc")])]});
            hole(context, id + "F18", {"style" : HoleStyle.SIMPLE, "endStyle" : HoleEndStyle.THROUGH, "holeDiameter" : 5 * mm, "locations" : qUnion([Q0, Q1, Q2, Q3]), "scope" : qUnion([Q4]), "tappedDepth" : 12 * mm, "tapClearance" : 3});
        }
        {
            var Q0;
            Q0=makeQuery(id+"F0.imprint","IMPRINT",FACE,{"disambiguationData":[TD([[makeQuery(id+"F0.imprint","IMPRINT",EDGE,{"derivedFrom":sQuery(id+"F0.wireOp",EDGE,"E119")}),1.0]])]});
            extrude(context, id + "F19", {"entities" : qUnion([Q0]), "depth" : 800 * mm});
        }
        {
            var Q0;
            Q0=sQuery(id+"F0.wireOp",VERTEX,"E127");
            var Q1;
            Q1=makeQuery(id+"F9.opExtrude","SWEPT_BODY",BODY,{"disambiguationData":[OSD([sQuery(id+"F0.wireOp",EDGE,"E15.top"),sQuery(id+"F0.wireOp",EDGE,"E15.bottom"),sQuery(id+"F0.wireOp",EDGE,"E15.right"),sQuery(id+"F0.wireOp",EDGE,"E15.left"),sQuery(id+"F0.wireOp",EDGE,"E16"),sQuery(id+"F0.wireOp",EDGE,"E17"),sQuery(id+"F0.wireOp",EDGE,"db127f97-5cef-414b-9448-db71186049b8"),sQuery(id+"F0.wireOp",EDGE,"E18"),sQuery(id+"F0.wireOp",EDGE,"8a787ebf-446f-4dcb-904e-3cfb27b04ef8"),sQuery(id+"F0.wireOp",EDGE,"ef12e896-fafc-46bc-9dbb-420634019300"),sQuery(id+"F0.wireOp",EDGE,"E19"),sQuery(id+"F0.wireOp",EDGE,"E20"),sQuery(id+"F0.wireOp",EDGE,"E21"),sQuery(id+"F0.wireOp",EDGE,"E22"),sQuery(id+"F0.wireOp",EDGE,"E23"),sQuery(id+"F0.wireOp",EDGE,"9d671b4d-fca4-4341-a421-3bffd57b6420"),sQuery(id+"F0.wireOp",EDGE,"E24"),sQuery(id+"F0.wireOp",EDGE,"12209c70-deae-4930-8f2c-ba15db2709be"),sQuery(id+"F0.wireOp",EDGE,"E25"),sQuery(id+"F0.wireOp",EDGE,"E26"),sQuery(id+"F0.wireOp",EDGE,"E27")])]});
            hole(context, id + "F20", {"style" : HoleStyle.SIMPLE, "endStyle" : HoleEndStyle.THROUGH, "oppositeDirection" : true, "holeDiameter" : 50 * mm, "locations" : qUnion([Q0]), "scope" : qUnion([Q1]), "isTappedThrough" : true});
        }
        {
            var Q0;
            Q0=sQuery(id+"F0.wireOp",VERTEX,"E131");
            var Q1;
            Q1=sQuery(id+"F0.wireOp",VERTEX,"E129");
            var Q2;
            Q2=sQuery(id+"F0.wireOp",VERTEX,"E132");
            var Q3;
            Q3=sQuery(id+"F0.wireOp",VERTEX,"E130");
            var Q4;
            Q4=makeQuery(id+"F9.opExtrude","SWEPT_BODY",BODY,{"disambiguationData":[OSD([sQuery(id+"F0.wireOp",EDGE,"E15.top"),sQuery(id+"F0.wireOp",EDGE,"E15.bottom"),sQuery(id+"F0.wireOp",EDGE,"E15.right"),sQuery(id+"F0.wireOp",EDGE,"E15.left"),sQuery(id+"F0.wireOp",EDGE,"E16"),sQuery(id+"F0.wireOp",EDGE,"E17"),sQuery(id+"F0.wireOp",EDGE,"db127f97-5cef-414b-9448-db71186049b8"),sQuery(id+"F0.wireOp",EDGE,"E18"),sQuery(id+"F0.wireOp",EDGE,"8a787ebf-446f-4dcb-904e-3cfb27b04ef8"),sQuery(id+"F0.wireOp",EDGE,"ef12e896-fafc-46bc-9dbb-420634019300"),sQuery(id+"F0.wireOp",EDGE,"E19"),sQuery(id+"F0.wireOp",EDGE,"E20"),sQuery(id+"F0.wireOp",EDGE,"E21"),sQuery(id+"F0.wireOp",EDGE,"E22"),sQuery(id+"F0.wireOp",EDGE,"E23"),sQuery(id+"F0.wireOp",EDGE,"9d671b4d-fca4-4341-a421-3bffd57b6420"),sQuery(id+"F0.wireOp",EDGE,"E24"),sQuery(id+"F0.wireOp",EDGE,"12209c70-deae-4930-8f2c-ba15db2709be"),sQuery(id+"F0.wireOp",EDGE,"E25"),sQuery(id+"F0.wireOp",EDGE,"E26"),sQuery(id+"F0.wireOp",EDGE,"E27")])]});
            hole(context, id + "F21", {"style" : HoleStyle.SIMPLE, "endStyle" : HoleEndStyle.THROUGH, "oppositeDirection" : true, "holeDiameter" : 4.2 * mm, "locations" : qUnion([Q0, Q1, Q2, Q3]), "scope" : qUnion([Q4]), "isTappedThrough" : true});
        }
        {
            var Q0;
            Q0=sQuery(id+"F0.wireOp",VERTEX,"E136");
            var Q1;
            Q1=sQuery(id+"F0.wireOp",VERTEX,"E135");
            var Q2;
            Q2=sQuery(id+"F0.wireOp",VERTEX,"E137");
            var Q3;
            Q3=sQuery(id+"F0.wireOp",VERTEX,"E138");
            var Q4;
            Q4=sQuery(id+"F0.wireOp",VERTEX,"E139");
            var Q5;
            Q5=sQuery(id+"F0.wireOp",VERTEX,"E140");
            var Q6;
            Q6=sQuery(id+"F0.wireOp",VERTEX,"E141");
            var Q7;
            Q7=sQuery(id+"F0.wireOp",VERTEX,"E142");
            var Q8;
            Q8=makeQuery(id+"F9.opExtrude","SWEPT_BODY",BODY,{"disambiguationData":[OSD([sQuery(id+"F0.wireOp",EDGE,"E15.top"),sQuery(id+"F0.wireOp",EDGE,"E15.bottom"),sQuery(id+"F0.wireOp",EDGE,"E15.right"),sQuery(id+"F0.wireOp",EDGE,"E15.left"),sQuery(id+"F0.wireOp",EDGE,"E16"),sQuery(id+"F0.wireOp",EDGE,"E17"),sQuery(id+"F0.wireOp",EDGE,"E18"),sQuery(id+"F0.wireOp",EDGE,"8a787ebf-446f-4dcb-904e-3cfb27b04ef8"),sQuery(id+"F0.wireOp",EDGE,"ef12e896-fafc-46bc-9dbb-420634019300"),sQuery(id+"F0.wireOp",EDGE,"E19"),sQuery(id+"F0.wireOp",EDGE,"E20"),sQuery(id+"F0.wireOp",EDGE,"E21"),sQuery(id+"F0.wireOp",EDGE,"E22"),sQuery(id+"F0.wireOp",EDGE,"E23"),sQuery(id+"F0.wireOp",EDGE,"9d671b4d-fca4-4341-a421-3bffd57b6420"),sQuery(id+"F0.wireOp",EDGE,"E24"),sQuery(id+"F0.wireOp",EDGE,"12209c70-deae-4930-8f2c-ba15db2709be"),sQuery(id+"F0.wireOp",EDGE,"E25"),sQuery(id+"F0.wireOp",EDGE,"E26"),sQuery(id+"F0.wireOp",EDGE,"E27")])]});
            hole(context, id + "F22", {"style" : HoleStyle.SIMPLE, "endStyle" : HoleEndStyle.THROUGH, "oppositeDirection" : true, "holeDiameter" : 8.4 * mm, "locations" : qUnion([Q0, Q1, Q2, Q3, Q4, Q5, Q6, Q7]), "scope" : qUnion([Q8]), "isTappedThrough" : true});
        }
        {
            var Q0;
            Q0=sQuery(id+"F0.wireOp",VERTEX,"E151");
            var Q1;
            Q1=sQuery(id+"F0.wireOp",VERTEX,"E144");
            var Q2;
            Q2=sQuery(id+"F0.wireOp",VERTEX,"E150");
            var Q3;
            Q3=sQuery(id+"F0.wireOp",VERTEX,"E145");
            var Q4;
            Q4=sQuery(id+"F0.wireOp",VERTEX,"E149");
            var Q5;
            Q5=sQuery(id+"F0.wireOp",VERTEX,"E146");
            var Q6;
            Q6=sQuery(id+"F0.wireOp",VERTEX,"E148");
            var Q7;
            Q7=sQuery(id+"F0.wireOp",VERTEX,"E147");
            var Q8;
            Q8=makeQuery(id+"F8.opExtrude","SWEPT_BODY",BODY,{"disambiguationData":[OSD([sQuery(id+"F0.wireOp",EDGE,"E2.bottom"),sQuery(id+"F0.wireOp",EDGE,"E2.top"),sQuery(id+"F0.wireOp",EDGE,"E2.left"),sQuery(id+"F0.wireOp",EDGE,"E2.right"),sQuery(id+"F0.wireOp",EDGE,"E3"),sQuery(id+"F0.wireOp",EDGE,"E4"),sQuery(id+"F0.wireOp",EDGE,"E5"),sQuery(id+"F0.wireOp",EDGE,"E6"),sQuery(id+"F0.wireOp",EDGE,"E7"),sQuery(id+"F0.wireOp",EDGE,"E8"),sQuery(id+"F0.wireOp",EDGE,"E9"),sQuery(id+"F0.wireOp",EDGE,"E10"),sQuery(id+"F0.wireOp",EDGE,"E11"),sQuery(id+"F0.wireOp",EDGE,"E12"),sQuery(id+"F0.wireOp",EDGE,"E13"),sQuery(id+"F0.wireOp",EDGE,"E14"),sQuery(id+"F0.wireOp",EDGE,"118e7f54-ae4d-4cc3-a0cb-1c85e96f6ff4"),sQuery(id+"F0.wireOp",EDGE,"b824cd55-5977-4451-85f6-8f819232337b"),sQuery(id+"F0.wireOp",EDGE,"f4b02ed7-cc01-4e7e-b6ab-ee6ed3c02ebc"),sQuery(id+"F0.wireOp",EDGE,"62a1acf6-454a-45f0-a1a5-7ebdd69a2e99"),sQuery(id+"F0.wireOp",EDGE,"db54ed66-e006-4cbb-8daf-ac18bcd11d0f")])]});
            hole(context, id + "F23", {"style" : HoleStyle.SIMPLE, "endStyle" : HoleEndStyle.THROUGH, "oppositeDirection" : true, "holeDiameter" : 8.4 * mm, "locations" : qUnion([Q0, Q1, Q2, Q3, Q4, Q5, Q6, Q7]), "scope" : qUnion([Q8]), "isTappedThrough" : true});
        }
        {
            var Q0;
            {var subQ0=sQuery(id+"F0.wireOp",EDGE,"E45");var subQ1=sQuery(id+"F0.wireOp",EDGE,"E0.bottom");var subQ2=sQuery(id+"F0.wireOp",EDGE,"E43");var subQ3=sQuery(id+"F0.wireOp",EDGE,"E42");var subQ4=sQuery(id+"F0.wireOp",EDGE,"E41");var subQ5=sQuery(id+"F0.wireOp",EDGE,"E40");var subQ6=sQuery(id+"F0.wireOp",EDGE,"E44");var subQ7=sQuery(id+"F0.wireOp",EDGE,"E0.right");var subQ8=sQuery(id+"F0.wireOp",EDGE,"E0.left");var subQ9=sQuery(id+"F0.wireOp",EDGE,"E49");var subQ10=sQuery(id+"F0.wireOp",EDGE,"E39");var subQ11=sQuery(id+"F0.wireOp",EDGE,"E46");var subQ12=sQuery(id+"F0.wireOp",EDGE,"E47");var subQ13=sQuery(id+"F0.wireOp",EDGE,"E48");Q0=makeQuery(id+"F13.boolean.opBoolean","SPLIT",FACE,{"disambiguationData":[TD([makeQuery(id+"F1.opExtrude","SWEPT_FACE",FACE,{"disambiguationData":[OSD([subQ1])]})])],"derivedFrom":makeQuery(id+"F1.opExtrude","CAP_FACE",FACE,{"disambiguationData":[OSD([subQ1,sQuery(id+"F0.wireOp",EDGE,"E0.top"),subQ8,subQ7,sQuery(id+"F0.wireOp",EDGE,"E28"),sQuery(id+"F0.wireOp",EDGE,"E29"),sQuery(id+"F0.wireOp",EDGE,"E30"),sQuery(id+"F0.wireOp",EDGE,"E31"),sQuery(id+"F0.wireOp",EDGE,"E32"),sQuery(id+"F0.wireOp",EDGE,"E33"),sQuery(id+"F0.wireOp",EDGE,"E34"),sQuery(id+"F0.wireOp",EDGE,"E35"),sQuery(id+"F0.wireOp",EDGE,"E36"),sQuery(id+"F0.wireOp",EDGE,"E37"),sQuery(id+"F0.wireOp",EDGE,"E38"),subQ10,subQ5,subQ4,subQ3,subQ2,subQ6,subQ0,subQ11,subQ12,subQ13,subQ9,sQuery(id+"F0.wireOp",EDGE,"E50"),sQuery(id+"F0.wireOp",EDGE,"E51"),sQuery(id+"F0.wireOp",EDGE,"E53"),sQuery(id+"F0.wireOp",EDGE,"E54"),sQuery(id+"F0.wireOp",EDGE,"E55"),sQuery(id+"F0.wireOp",EDGE,"E56")])],"isStart":false})});}
            var sketch = newSketch(context, id + "F24", { "sketchPlane" : qUnion([Q0])});
            skLineSegment(sketch, "E218", {"start": v(436.31, 40.5) * mm, "end": v(-316.17, 40.5) * mm});
            skLineSegment(sketch, "E219", {"start": v(-316.17, -94.5) * mm, "end": v(441.17, -94.5) * mm});
            skPoint(sketch, "E220", {"position": v(429.62, 40.5) * mm});
            skPoint(sketch, "E221", {"position": v(429.62, -94.5) * mm});
            skPoint(sketch, "E222", {"position": v(-305.38, 40.5) * mm});
            skPoint(sketch, "E223", {"position": v(-305.38, -94.5) * mm});
            skPoint(sketch, "E224", {"position": v(-267.88, 40.5) * mm});
            skPoint(sketch, "E225", {"position": v(-267.88, -94.5) * mm});
            skPoint(sketch, "E226", {"position": v(-207.88, 40.5) * mm});
            skPoint(sketch, "E227", {"position": v(-207.88, -94.5) * mm});
            skPoint(sketch, "E228", {"position": v(-147.88, 40.5) * mm});
            skPoint(sketch, "E229", {"position": v(-147.88, -94.5) * mm});
            skPoint(sketch, "E230", {"position": v(-87.88, 40.5) * mm});
            skPoint(sketch, "E231", {"position": v(-87.88, -94.5) * mm});
            skPoint(sketch, "E232", {"position": v(-27.88, 40.5) * mm});
            skPoint(sketch, "E233", {"position": v(-27.88, -94.5) * mm});
            skPoint(sketch, "E234", {"position": v(32.12, 40.5) * mm});
            skPoint(sketch, "E235", {"position": v(32.12, -94.5) * mm});
            skPoint(sketch, "E236", {"position": v(92.12, 40.5) * mm});
            skPoint(sketch, "E237", {"position": v(92.12, -94.5) * mm});
            skPoint(sketch, "E238", {"position": v(152.12, 40.5) * mm});
            skPoint(sketch, "E239", {"position": v(212.12, 40.5) * mm});
            skPoint(sketch, "E240", {"position": v(272.12, 40.5) * mm});
            skPoint(sketch, "E241", {"position": v(332.12, 40.5) * mm});
            skPoint(sketch, "E242", {"position": v(392.12, 40.5) * mm});
            skPoint(sketch, "E243", {"position": v(392.12, -94.5) * mm});
            skPoint(sketch, "E244", {"position": v(332.12, -94.5) * mm});
            skPoint(sketch, "E245", {"position": v(272.12, -94.5) * mm});
            skPoint(sketch, "E246", {"position": v(212.12, -94.5) * mm});
            skPoint(sketch, "E247", {"position": v(152.12, -94.5) * mm});
            skSolve(sketch);
        }
        {
            var Q0;
            Q0=sQuery(id+"F24.wireOp",VERTEX,"E222");
            var Q1;
            Q1=sQuery(id+"F24.wireOp",VERTEX,"E223");
            var Q2;
            Q2=sQuery(id+"F24.wireOp",VERTEX,"E224");
            var Q3;
            Q3=sQuery(id+"F24.wireOp",VERTEX,"E225");
            var Q4;
            Q4=sQuery(id+"F24.wireOp",VERTEX,"E226");
            var Q5;
            Q5=sQuery(id+"F24.wireOp",VERTEX,"E227");
            var Q6;
            Q6=sQuery(id+"F24.wireOp",VERTEX,"E228");
            var Q7;
            Q7=sQuery(id+"F24.wireOp",VERTEX,"E229");
            var Q8;
            Q8=sQuery(id+"F24.wireOp",VERTEX,"E230");
            var Q9;
            Q9=sQuery(id+"F24.wireOp",VERTEX,"E231");
            var Q10;
            Q10=sQuery(id+"F24.wireOp",VERTEX,"E232");
            var Q11;
            Q11=sQuery(id+"F24.wireOp",VERTEX,"E233");
            var Q12;
            Q12=sQuery(id+"F24.wireOp",VERTEX,"E235");
            var Q13;
            Q13=sQuery(id+"F24.wireOp",VERTEX,"E237");
            var Q14;
            Q14=sQuery(id+"F24.wireOp",VERTEX,"E247");
            var Q15;
            Q15=sQuery(id+"F24.wireOp",VERTEX,"E246");
            var Q16;
            Q16=sQuery(id+"F24.wireOp",VERTEX,"E234");
            var Q17;
            Q17=sQuery(id+"F24.wireOp",VERTEX,"E236");
            var Q18;
            Q18=sQuery(id+"F24.wireOp",VERTEX,"E238");
            var Q19;
            Q19=sQuery(id+"F24.wireOp",VERTEX,"E239");
            var Q20;
            Q20=sQuery(id+"F24.wireOp",VERTEX,"E240");
            var Q21;
            Q21=sQuery(id+"F24.wireOp",VERTEX,"E241");
            var Q22;
            Q22=sQuery(id+"F24.wireOp",VERTEX,"E242");
            var Q23;
            Q23=sQuery(id+"F24.wireOp",VERTEX,"E220");
            var Q24;
            Q24=sQuery(id+"F24.wireOp",VERTEX,"E245");
            var Q25;
            Q25=sQuery(id+"F24.wireOp",VERTEX,"E244");
            var Q26;
            Q26=sQuery(id+"F24.wireOp",VERTEX,"E243");
            var Q27;
            Q27=sQuery(id+"F24.wireOp",VERTEX,"E221");
            var Q28;
            Q28=makeQuery(id+"F1.opExtrude","SWEPT_BODY",BODY,{"disambiguationData":[OSD([sQuery(id+"F0.wireOp",EDGE,"E0.bottom"),sQuery(id+"F0.wireOp",EDGE,"E0.top"),sQuery(id+"F0.wireOp",EDGE,"E0.left"),sQuery(id+"F0.wireOp",EDGE,"E0.right"),sQuery(id+"F0.wireOp",EDGE,"E28"),sQuery(id+"F0.wireOp",EDGE,"E29"),sQuery(id+"F0.wireOp",EDGE,"E30"),sQuery(id+"F0.wireOp",EDGE,"E31"),sQuery(id+"F0.wireOp",EDGE,"E32"),sQuery(id+"F0.wireOp",EDGE,"E33"),sQuery(id+"F0.wireOp",EDGE,"E34"),sQuery(id+"F0.wireOp",EDGE,"E35"),sQuery(id+"F0.wireOp",EDGE,"E36"),sQuery(id+"F0.wireOp",EDGE,"E37"),sQuery(id+"F0.wireOp",EDGE,"E38"),sQuery(id+"F0.wireOp",EDGE,"E39"),sQuery(id+"F0.wireOp",EDGE,"E40"),sQuery(id+"F0.wireOp",EDGE,"E41"),sQuery(id+"F0.wireOp",EDGE,"E42"),sQuery(id+"F0.wireOp",EDGE,"E43"),sQuery(id+"F0.wireOp",EDGE,"E44"),sQuery(id+"F0.wireOp",EDGE,"E45"),sQuery(id+"F0.wireOp",EDGE,"E46"),sQuery(id+"F0.wireOp",EDGE,"E47"),sQuery(id+"F0.wireOp",EDGE,"E48"),sQuery(id+"F0.wireOp",EDGE,"E49"),sQuery(id+"F0.wireOp",EDGE,"E50"),sQuery(id+"F0.wireOp",EDGE,"E51"),sQuery(id+"F0.wireOp",EDGE,"E53"),sQuery(id+"F0.wireOp",EDGE,"E54"),sQuery(id+"F0.wireOp",EDGE,"E55"),sQuery(id+"F0.wireOp",EDGE,"E56")])]});
            hole(context, id + "F25", {"style" : HoleStyle.C_BORE, "endStyle" : HoleEndStyle.THROUGH, "holeDiameter" : 8.4 * mm, "cBoreDiameter" : 14 * mm, "cBoreDepth" : 9 * mm, "tappedDepth" : 12 * mm, "tapClearance" : 3, "locations" : qUnion([Q0, Q1, Q2, Q3, Q4, Q5, Q6, Q7, Q8, Q9, Q10, Q11, Q12, Q13, Q14, Q15, Q16, Q17, Q18, Q19, Q20, Q21, Q22, Q23, Q24, Q25, Q26, Q27]), "scope" : qUnion([Q28])});
        }
        {
            var Q0;
            Q0=makeQuery(id+"F0.imprint","IMPRINT",FACE,{"disambiguationData":[TD([[makeQuery(id+"F0.imprint","IMPRINT",EDGE,{"derivedFrom":sQuery(id+"F0.wireOp",EDGE,"E106")}),1.0]])]});
            var sketch = newSketch(context, id + "F26", { "sketchPlane" : qUnion([Q0])});
            skLineSegment(sketch, "E248", {"start": v(-411.9, -429.68) * mm, "end": v(344.54, -429.68) * mm});
            skLineSegment(sketch, "E249", {"start": v(344.54, -384.68) * mm, "end": v(-411.9, -384.68) * mm});
            skPoint(sketch, "E250", {"position": v(334.69, -429.68) * mm});
            skPoint(sketch, "E251", {"position": v(297.19, -429.68) * mm});
            skPoint(sketch, "E252", {"position": v(237.19, -429.68) * mm});
            skPoint(sketch, "E253", {"position": v(177.19, -429.68) * mm});
            skPoint(sketch, "E254", {"position": v(57.19, -429.68) * mm});
            skPoint(sketch, "E255", {"position": v(-2.81, -429.68) * mm});
            skPoint(sketch, "E256", {"position": v(-62.81, -429.68) * mm});
            skPoint(sketch, "E257", {"position": v(-182.81, -429.68) * mm});
            skPoint(sketch, "E258", {"position": v(-242.81, -429.68) * mm});
            skPoint(sketch, "E259", {"position": v(-302.81, -429.68) * mm});
            skPoint(sketch, "E260", {"position": v(-362.81, -429.68) * mm});
            skPoint(sketch, "E261", {"position": v(117.19, -429.68) * mm});
            skPoint(sketch, "E262", {"position": v(-122.81, -429.68) * mm});
            skPoint(sketch, "E263", {"position": v(-400.31, -429.68) * mm});
            skPoint(sketch, "E264", {"position": v(267.19, -384.68) * mm});
            skPoint(sketch, "E265", {"position": v(207.19, -384.68) * mm});
            skPoint(sketch, "E266", {"position": v(147.19, -384.68) * mm});
            skPoint(sketch, "E267", {"position": v(87.19, -384.68) * mm});
            skPoint(sketch, "E268", {"position": v(27.19, -384.68) * mm});
            skPoint(sketch, "E269", {"position": v(-32.81, -384.68) * mm});
            skPoint(sketch, "E270", {"position": v(-92.81, -384.68) * mm});
            skPoint(sketch, "E271", {"position": v(-152.81, -384.68) * mm});
            skPoint(sketch, "E272", {"position": v(-212.81, -384.68) * mm});
            skPoint(sketch, "E273", {"position": v(-272.81, -384.68) * mm});
            skPoint(sketch, "E274", {"position": v(-332.81, -384.68) * mm});
            skPoint(sketch, "E275", {"position": v(-392.81, -384.68) * mm});
            skPoint(sketch, "E276", {"position": v(327.19, -384.68) * mm});
            skSolve(sketch);
        }
        {
            var Q0;
            Q0=sQuery(id+"F26.wireOp",VERTEX,"E250");
            var Q1;
            Q1=sQuery(id+"F26.wireOp",VERTEX,"E276");
            var Q2;
            Q2=sQuery(id+"F26.wireOp",VERTEX,"E264");
            var Q3;
            Q3=sQuery(id+"F26.wireOp",VERTEX,"E252");
            var Q4;
            Q4=sQuery(id+"F26.wireOp",VERTEX,"E265");
            var Q5;
            Q5=sQuery(id+"F26.wireOp",VERTEX,"E253");
            var Q6;
            Q6=sQuery(id+"F26.wireOp",VERTEX,"E266");
            var Q7;
            Q7=sQuery(id+"F26.wireOp",VERTEX,"E261");
            var Q8;
            Q8=sQuery(id+"F26.wireOp",VERTEX,"E267");
            var Q9;
            Q9=sQuery(id+"F26.wireOp",VERTEX,"E254");
            var Q10;
            Q10=sQuery(id+"F26.wireOp",VERTEX,"E268");
            var Q11;
            Q11=sQuery(id+"F26.wireOp",VERTEX,"E255");
            var Q12;
            Q12=sQuery(id+"F26.wireOp",VERTEX,"E269");
            var Q13;
            Q13=sQuery(id+"F26.wireOp",VERTEX,"E256");
            var Q14;
            Q14=sQuery(id+"F26.wireOp",VERTEX,"E270");
            var Q15;
            Q15=sQuery(id+"F26.wireOp",VERTEX,"E262");
            var Q16;
            Q16=sQuery(id+"F26.wireOp",VERTEX,"E257");
            var Q17;
            Q17=sQuery(id+"F26.wireOp",VERTEX,"E258");
            var Q18;
            Q18=sQuery(id+"F26.wireOp",VERTEX,"E259");
            var Q19;
            Q19=sQuery(id+"F26.wireOp",VERTEX,"E273");
            var Q20;
            Q20=sQuery(id+"F26.wireOp",VERTEX,"E272");
            var Q21;
            Q21=sQuery(id+"F26.wireOp",VERTEX,"E271");
            var Q22;
            Q22=sQuery(id+"F26.wireOp",VERTEX,"E274");
            var Q23;
            Q23=sQuery(id+"F26.wireOp",VERTEX,"E275");
            var Q24;
            Q24=sQuery(id+"F26.wireOp",VERTEX,"E263");
            var Q25;
            Q25=makeQuery(id+"F15.opExtrude","SWEPT_BODY",BODY,{"disambiguationData":[OSD([sQuery(id+"F0.wireOp",EDGE,"E106"),sQuery(id+"F0.wireOp",EDGE,"E107"),sQuery(id+"F0.wireOp",EDGE,"E108"),sQuery(id+"F0.wireOp",EDGE,"E109"),sQuery(id+"F0.wireOp",EDGE,"E110"),sQuery(id+"F0.wireOp",EDGE,"E111"),sQuery(id+"F0.wireOp",EDGE,"E112"),sQuery(id+"F0.wireOp",EDGE,"E113"),sQuery(id+"F0.wireOp",EDGE,"0buerCJm-Lt2G-jJo9-9LwQ-wygei9gSLH8x"),sQuery(id+"F0.wireOp",EDGE,"Cyo2l2n8-YYKy-Kl9p-W61Z-JTT53oPBxWLL"),sQuery(id+"F0.wireOp",EDGE,"L2AfWR9S-dHOE-b34O-2OkN-z4aWcMazjyWb"),sQuery(id+"F0.wireOp",EDGE,"E114"),sQuery(id+"F0.wireOp",EDGE,"E115.filletArc"),sQuery(id+"F0.wireOp",EDGE,"E116.filletArc"),sQuery(id+"F0.wireOp",EDGE,"E117.filletArc"),sQuery(id+"F0.wireOp",EDGE,"E118.filletArc")])]});
            hole(context, id + "F27", {"style" : HoleStyle.C_BORE, "endStyle" : HoleEndStyle.THROUGH, "oppositeDirection" : true, "holeDiameter" : 8.4 * mm, "cBoreDiameter" : 14 * mm, "cBoreDepth" : 11 * mm, "tappedDepth" : 12 * mm, "tapClearance" : 3, "locations" : qUnion([Q0, Q1, Q2, Q3, Q4, Q5, Q6, Q7, Q8, Q9, Q10, Q11, Q12, Q13, Q14, Q15, Q16, Q17, Q18, Q19, Q20, Q21, Q22, Q23, Q24]), "scope" : qUnion([Q25])});
        }
        {
            var Q0;
            Q0=sQuery(id+"F3.wireOp",VERTEX,"E164");
            var Q1;
            Q1=sQuery(id+"F3.wireOp",VERTEX,"E174");
            var Q2;
            Q2=sQuery(id+"F3.wireOp",VERTEX,"E163");
            var Q3;
            Q3=sQuery(id+"F3.wireOp",VERTEX,"E173");
            var Q4;
            Q4=sQuery(id+"F3.wireOp",VERTEX,"E162");
            var Q5;
            Q5=sQuery(id+"F3.wireOp",VERTEX,"E172");
            var Q6;
            Q6=sQuery(id+"F3.wireOp",VERTEX,"E161");
            var Q7;
            Q7=sQuery(id+"F3.wireOp",VERTEX,"E171");
            var Q8;
            Q8=sQuery(id+"F3.wireOp",VERTEX,"E160");
            var Q9;
            Q9=sQuery(id+"F3.wireOp",VERTEX,"E170");
            var Q10;
            Q10=sQuery(id+"F3.wireOp",VERTEX,"E165");
            var Q11;
            Q11=sQuery(id+"F3.wireOp",VERTEX,"E175");
            var Q12;
            Q12=sQuery(id+"F3.wireOp",VERTEX,"E166");
            var Q13;
            Q13=sQuery(id+"F3.wireOp",VERTEX,"E176");
            var Q14;
            Q14=sQuery(id+"F3.wireOp",VERTEX,"E167");
            var Q15;
            Q15=sQuery(id+"F3.wireOp",VERTEX,"E168");
            var Q16;
            Q16=sQuery(id+"F3.wireOp",VERTEX,"E177");
            var Q17;
            Q17=makeQuery(id+"F2.opExtrude","SWEPT_BODY",BODY,{"disambiguationData":[OSD([sQuery(id+"F0.wireOp",EDGE,"E1.right"),sQuery(id+"F0.wireOp",EDGE,"E1.left"),sQuery(id+"F0.wireOp",EDGE,"E1.top"),sQuery(id+"F0.wireOp",EDGE,"E1.bottom")])]});
            hole(context, id + "F28", {"style" : HoleStyle.SIMPLE, "endStyle" : HoleEndStyle.THROUGH, "holeDiameter" : 8.4 * mm, "tappedDepth" : 12 * mm, "tapClearance" : 3, "locations" : qUnion([Q0, Q1, Q2, Q3, Q4, Q5, Q6, Q7, Q8, Q9, Q10, Q11, Q12, Q13, Q14, Q15, Q16]), "scope" : qUnion([Q17])});
        }
        {
            var Q0;
            Q0=makeQuery(id+"F13.boolean.opBoolean","COPY",FACE,{"derivedFrom":makeQuery(id+"F13.opExtrude","CAP_FACE",FACE,{"disambiguationData":[OSD([sQuery(id+"F0.wireOp",EDGE,"E50"),sQuery(id+"F0.wireOp",EDGE,"E51"),sQuery(id+"F0.wireOp",EDGE,"E53"),sQuery(id+"F0.wireOp",EDGE,"E54"),sQuery(id+"F0.wireOp",EDGE,"E55"),sQuery(id+"F0.wireOp",EDGE,"E56"),sQuery(id+"F12.wireOp",EDGE,"E190.bottom"),sQuery(id+"F12.wireOp",EDGE,"E190.top"),sQuery(id+"F12.wireOp",EDGE,"E190.right"),sQuery(id+"F12.wireOp",EDGE,"E190.left")])],"isStart":false})});
            var sketch = newSketch(context, id + "F29", { "sketchPlane" : qUnion([Q0])});
            skPoint(sketch, "E277", {"position": v(-195.38, -55) * mm});
            skPoint(sketch, "E278", {"position": v(-195.38, -48) * mm});
            skPoint(sketch, "E279", {"position": v(-185.38, 1) * mm});
            skPoint(sketch, "E280", {"position": v(-185.38, -6) * mm});
            skPoint(sketch, "E281", {"position": v(-165.38, -48) * mm});
            skPoint(sketch, "E282", {"position": v(-165.38, -55) * mm});
            skPoint(sketch, "E283", {"position": v(339.62, 1) * mm});
            skPoint(sketch, "E284", {"position": v(339.62, -6) * mm});
            skSolve(sketch);
        }
        {
            var Q0;
            Q0=sQuery(id+"F29.wireOp",VERTEX,"E279");
            var Q1;
            Q1=sQuery(id+"F29.wireOp",VERTEX,"E280");
            var Q2;
            Q2=sQuery(id+"F29.wireOp",VERTEX,"E278");
            var Q3;
            Q3=sQuery(id+"F29.wireOp",VERTEX,"E277");
            var Q4;
            Q4=sQuery(id+"F29.wireOp",VERTEX,"E281");
            var Q5;
            Q5=sQuery(id+"F29.wireOp",VERTEX,"E282");
            var Q6;
            Q6=sQuery(id+"F29.wireOp",VERTEX,"E283");
            var Q7;
            Q7=sQuery(id+"F29.wireOp",VERTEX,"E284");
            var Q8;
            Q8=makeQuery(id+"F1.opExtrude","SWEPT_BODY",BODY,{"disambiguationData":[OSD([sQuery(id+"F0.wireOp",EDGE,"E0.bottom"),sQuery(id+"F0.wireOp",EDGE,"E0.top"),sQuery(id+"F0.wireOp",EDGE,"E0.left"),sQuery(id+"F0.wireOp",EDGE,"E0.right"),sQuery(id+"F0.wireOp",EDGE,"E28"),sQuery(id+"F0.wireOp",EDGE,"E29"),sQuery(id+"F0.wireOp",EDGE,"E30"),sQuery(id+"F0.wireOp",EDGE,"E31"),sQuery(id+"F0.wireOp",EDGE,"E32"),sQuery(id+"F0.wireOp",EDGE,"E33"),sQuery(id+"F0.wireOp",EDGE,"E34"),sQuery(id+"F0.wireOp",EDGE,"E35"),sQuery(id+"F0.wireOp",EDGE,"E36"),sQuery(id+"F0.wireOp",EDGE,"E37"),sQuery(id+"F0.wireOp",EDGE,"E38"),sQuery(id+"F0.wireOp",EDGE,"E39"),sQuery(id+"F0.wireOp",EDGE,"E40"),sQuery(id+"F0.wireOp",EDGE,"E41"),sQuery(id+"F0.wireOp",EDGE,"E42"),sQuery(id+"F0.wireOp",EDGE,"E43"),sQuery(id+"F0.wireOp",EDGE,"E44"),sQuery(id+"F0.wireOp",EDGE,"E45"),sQuery(id+"F0.wireOp",EDGE,"E46"),sQuery(id+"F0.wireOp",EDGE,"E47"),sQuery(id+"F0.wireOp",EDGE,"E48"),sQuery(id+"F0.wireOp",EDGE,"E49"),sQuery(id+"F0.wireOp",EDGE,"E50"),sQuery(id+"F0.wireOp",EDGE,"E51"),sQuery(id+"F0.wireOp",EDGE,"E53"),sQuery(id+"F0.wireOp",EDGE,"E54"),sQuery(id+"F0.wireOp",EDGE,"E55"),sQuery(id+"F0.wireOp",EDGE,"E56")])]});
            hole(context, id + "F30", {"style" : HoleStyle.SIMPLE, "endStyle" : HoleEndStyle.THROUGH, "holeDiameter" : 2.5 * mm, "isTappedThrough" : true, "tappedDepth" : 12 * mm, "tapClearance" : 3, "locations" : qUnion([Q0, Q1, Q2, Q3, Q4, Q5, Q6, Q7]), "scope" : qUnion([Q8])});
        }
        {
            var Q0;
            Q0=makeQuery(id+"F1.opExtrude","SWEPT_FACE",FACE,{"disambiguationData":[OSD([sQuery(id+"F0.wireOp",EDGE,"E0.top")])]});
            var sketch = newSketch(context, id + "F31", { "sketchPlane" : qUnion([Q0])});
            skPoint(sketch, "E285", {"position": v(-240.38, 9) * mm});
            skPoint(sketch, "E286", {"position": v(364.62, 9) * mm});
            skPoint(sketch, "E287", {"position": v(62.12, 9) * mm});
            skSolve(sketch);
        }
        {
            var Q0;
            Q0=sQuery(id+"F31.wireOp",VERTEX,"E285");
            var Q1;
            Q1=sQuery(id+"F31.wireOp",VERTEX,"E287");
            var Q2;
            Q2=sQuery(id+"F31.wireOp",VERTEX,"E286");
            var Q3;
            Q3=makeQuery(id+"F1.opExtrude","SWEPT_BODY",BODY,{"disambiguationData":[OSD([sQuery(id+"F0.wireOp",EDGE,"E0.bottom"),sQuery(id+"F0.wireOp",EDGE,"E0.top"),sQuery(id+"F0.wireOp",EDGE,"E0.left"),sQuery(id+"F0.wireOp",EDGE,"E0.right"),sQuery(id+"F0.wireOp",EDGE,"E28"),sQuery(id+"F0.wireOp",EDGE,"E29"),sQuery(id+"F0.wireOp",EDGE,"E30"),sQuery(id+"F0.wireOp",EDGE,"E31"),sQuery(id+"F0.wireOp",EDGE,"E32"),sQuery(id+"F0.wireOp",EDGE,"E33"),sQuery(id+"F0.wireOp",EDGE,"E34"),sQuery(id+"F0.wireOp",EDGE,"E35"),sQuery(id+"F0.wireOp",EDGE,"E36"),sQuery(id+"F0.wireOp",EDGE,"E37"),sQuery(id+"F0.wireOp",EDGE,"E38"),sQuery(id+"F0.wireOp",EDGE,"E39"),sQuery(id+"F0.wireOp",EDGE,"E40"),sQuery(id+"F0.wireOp",EDGE,"E41"),sQuery(id+"F0.wireOp",EDGE,"E42"),sQuery(id+"F0.wireOp",EDGE,"E43"),sQuery(id+"F0.wireOp",EDGE,"E44"),sQuery(id+"F0.wireOp",EDGE,"E45"),sQuery(id+"F0.wireOp",EDGE,"E46"),sQuery(id+"F0.wireOp",EDGE,"E47"),sQuery(id+"F0.wireOp",EDGE,"E48"),sQuery(id+"F0.wireOp",EDGE,"E49"),sQuery(id+"F0.wireOp",EDGE,"E50"),sQuery(id+"F0.wireOp",EDGE,"E51"),sQuery(id+"F0.wireOp",EDGE,"E53"),sQuery(id+"F0.wireOp",EDGE,"E54"),sQuery(id+"F0.wireOp",EDGE,"E55"),sQuery(id+"F0.wireOp",EDGE,"E56")])]});
            hole(context, id + "F32", {"style" : HoleStyle.SIMPLE, "endStyle" : HoleEndStyle.BLIND, "holeDiameter" : 5 * mm, "holeDepth" : 12 * mm, "tappedDepth" : 12 * mm, "tapClearance" : 3, "locations" : qUnion([Q0, Q1, Q2]), "scope" : qUnion([Q3])});
        }
        {
            var Q0;
            Q0=sQuery(id+"F16.wireOp",VERTEX,"E215");
            var Q1;
            Q1=sQuery(id+"F16.wireOp",VERTEX,"E213");
            var Q2;
            Q2=sQuery(id+"F16.wireOp",VERTEX,"E214");
            var Q3;
            Q3=makeQuery(id+"F15.opExtrude","SWEPT_BODY",BODY,{"disambiguationData":[OSD([sQuery(id+"F0.wireOp",EDGE,"E106"),sQuery(id+"F0.wireOp",EDGE,"E107"),sQuery(id+"F0.wireOp",EDGE,"E108"),sQuery(id+"F0.wireOp",EDGE,"E109"),sQuery(id+"F0.wireOp",EDGE,"E110"),sQuery(id+"F0.wireOp",EDGE,"E111"),sQuery(id+"F0.wireOp",EDGE,"E112"),sQuery(id+"F0.wireOp",EDGE,"E113"),sQuery(id+"F0.wireOp",EDGE,"E114"),sQuery(id+"F0.wireOp",EDGE,"E117.filletArc"),sQuery(id+"F0.wireOp",EDGE,"E118.filletArc"),sQuery(id+"F0.wireOp",EDGE,"E152"),sQuery(id+"F0.wireOp",EDGE,"E153"),sQuery(id+"F0.wireOp",EDGE,"E154"),sQuery(id+"F0.wireOp",EDGE,"E157.filletArc"),sQuery(id+"F0.wireOp",EDGE,"E158.filletArc")])]});
            hole(context, id + "F33", {"style" : HoleStyle.SIMPLE, "endStyle" : HoleEndStyle.BLIND, "holeDiameter" : 5 * mm, "holeDepth" : 10 * mm, "tappedDepth" : 12 * mm, "tapClearance" : 3, "locations" : qUnion([Q0, Q1, Q2]), "scope" : qUnion([Q3])});
        }
    });
